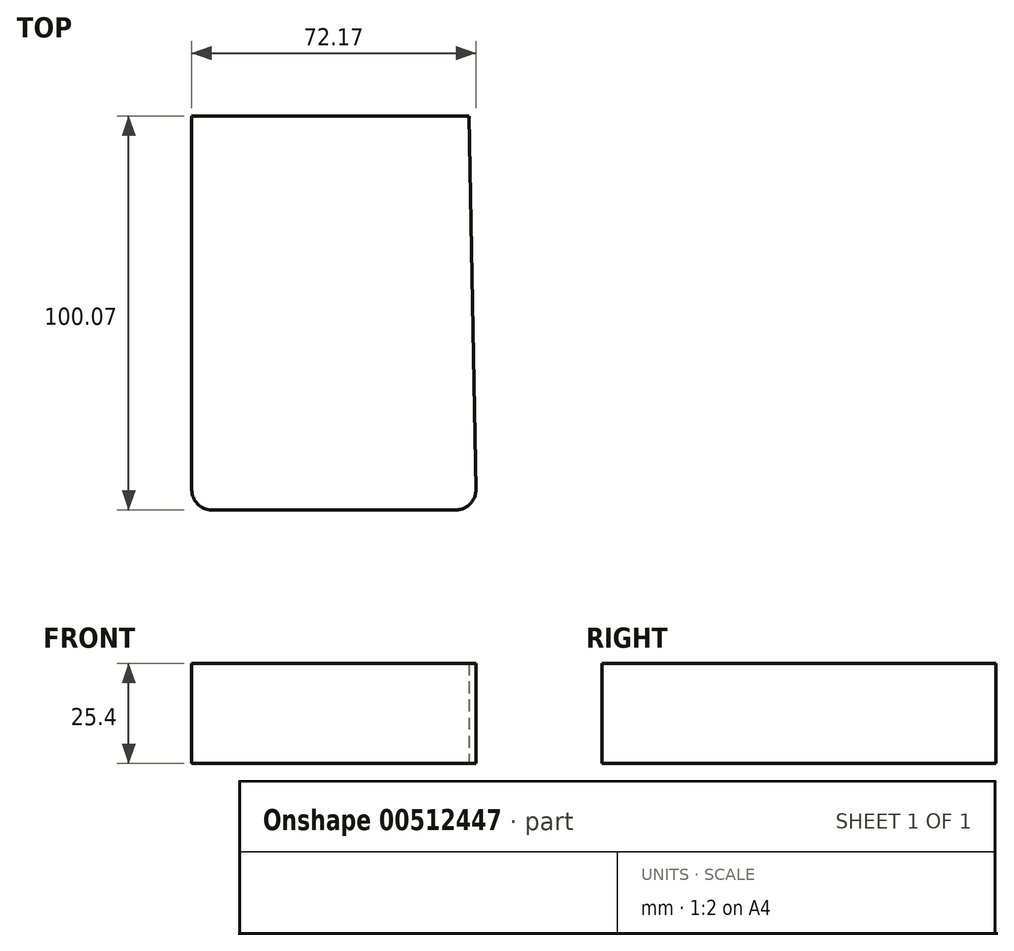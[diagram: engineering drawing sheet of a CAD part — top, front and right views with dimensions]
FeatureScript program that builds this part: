
annotation { "Feature Type Name" : "Feature", "Feature Type Description" : "" }
export const myFeature = defineFeature(function(context is Context, id is Id, definition is map)
    precondition{}
    {
        {
            var Q0;
            Q0=qCreatedBy(makeId("Top.planeOp"),FACE);
            var sketch = newSketch(context, id + "F0", { "sketchPlane" : qUnion([Q0])});
            skLineSegment(sketch, "E0", {"start": v(24.92, 47.55) * mm, "end": v(-45.5, 47.55) * mm});
            skLineSegment(sketch, "E1", {"start": v(-45.5, 47.55) * mm, "end": v(-45.5, -52.52) * mm});
            skLineSegment(sketch, "E2", {"start": v(-45.5, -52.52) * mm, "end": v(26.77, -52.52) * mm});
            skLineSegment(sketch, "E3", {"start": v(26.77, -52.52) * mm, "end": v(24.92, 47.55) * mm});
            skSolve(sketch);
        }
        {
            var Q0;
            Q0=makeQuery(id+"F0.imprint","IMPRINT",FACE,{"disambiguationData":[TD([[makeQuery(id+"F0.imprint","IMPRINT",EDGE,{"derivedFrom":sQuery(id+"F0.wireOp",EDGE,"E0")}),1.0]])]});
            extrude(context, id + "F1", {"entities" : qUnion([Q0]), "depth" : 25.4 * mm, "offsetDistance" : 25.4 * mm});
        }
        {
            var Q0;
            Q0=makeQuery(id+"F1.opExtrude","SWEPT_EDGE",EDGE,{"disambiguationData":[OSD([sQuery(id+"F0.wireOp",EDGE,"E2"),sQuery(id+"F0.wireOp",EDGE,"E3")])]});
            var Q1;
            Q1=makeQuery(id+"F1.opExtrude","SWEPT_EDGE",EDGE,{"disambiguationData":[OSD([sQuery(id+"F0.wireOp",EDGE,"E1"),sQuery(id+"F0.wireOp",EDGE,"E2")])]});
            fillet(context, id + "F2", {"entities" : qUnion([Q0, Q1]), "radius" : 5.08 * mm, "tangentPropagation" : true, "allowEdgeOverflow" : false});
        }
    });
